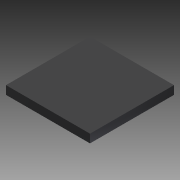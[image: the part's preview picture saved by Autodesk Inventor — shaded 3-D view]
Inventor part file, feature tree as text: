
AUTODESK INVENTOR PART (.ipt)
format: ipt  version: 2016 (Build 200138000, 138)  size: 81,920 bytes
history: native  units: in
note: dims shown in document units (in); Inventor stores cm internally (conversion verified against a paired STEP export)
features: extrude x1, sketch x1
ambient origin geometry x8: Origin, YZ Plane, XZ Plane, XY Plane, X Axis, Y Axis, Z Axis, Center Point
bodies: Solid1 (feature_tree)
feature tree (2):
  extrude  "Extrusion1"  Depth=1.0in
  sketch  "Sketch1"  dims[d0=1.0in d2=1.0in d3=0.1in d4=0.0in]
